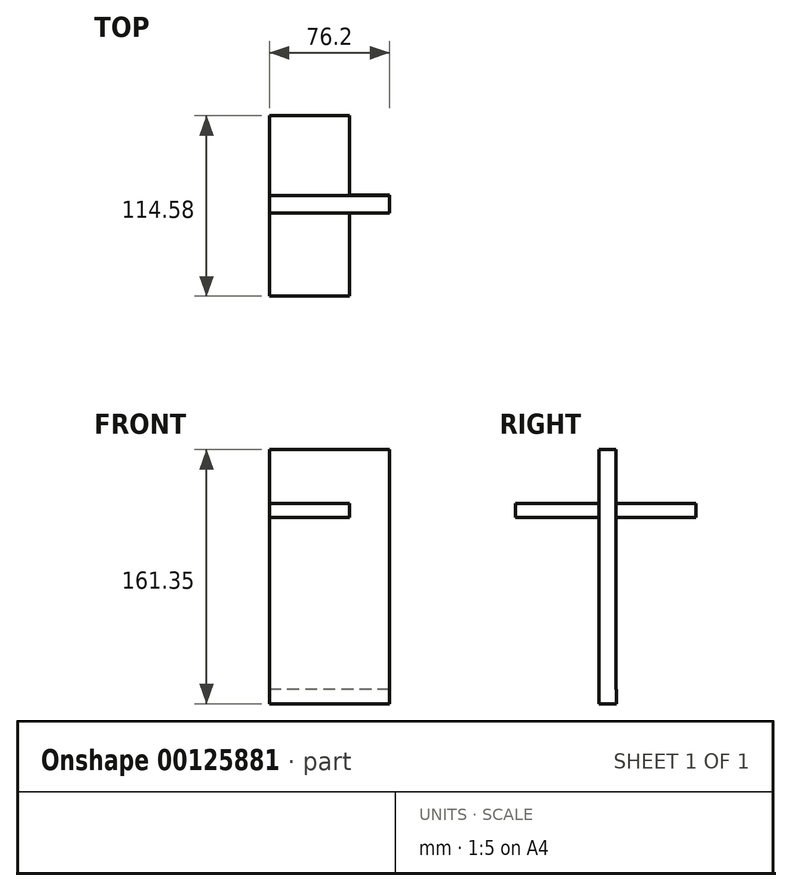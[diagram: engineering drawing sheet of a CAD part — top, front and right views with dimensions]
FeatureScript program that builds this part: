
annotation { "Feature Type Name" : "Feature", "Feature Type Description" : "" }
export const myFeature = defineFeature(function(context is Context, id is Id, definition is map)
    precondition{}
    {
        {
            var Q0;
            Q0=qCreatedBy(makeId("Right.planeOp"),FACE);
            var sketch = newSketch(context, id + "F0", { "sketchPlane" : qUnion([Q0])});
            skLineSegment(sketch, "E0.bottom", {"start": v(-22.48, 69.18) * mm, "end": v(-11.48, 69.18) * mm});
            skLineSegment(sketch, "E0.top", {"start": v(-22.48, -76.62) * mm, "end": v(-11.48, -76.62) * mm});
            skLineSegment(sketch, "E0.left", {"start": v(-22.48, 69.18) * mm, "end": v(-22.48, -76.62) * mm});
            skLineSegment(sketch, "E0.right", {"start": v(-11.48, 69.18) * mm, "end": v(-11.48, -76.62) * mm});
            skLineSegment(sketch, "E1.bottom", {"start": v(-11.48, 69.18) * mm, "end": v(-22.48, 69.18) * mm});
            skLineSegment(sketch, "E1.top", {"start": v(-11.48, 75.6) * mm, "end": v(-22.48, 75.6) * mm});
            skLineSegment(sketch, "E1.left", {"start": v(-11.48, 69.18) * mm, "end": v(-11.48, 75.6) * mm});
            skLineSegment(sketch, "E1.right", {"start": v(-22.48, 69.18) * mm, "end": v(-22.48, 75.6) * mm});
            skLineSegment(sketch, "E2.bottom", {"start": v(-22.48, -76.62) * mm, "end": v(-11.24, -76.62) * mm});
            skLineSegment(sketch, "E2.top", {"start": v(-22.48, -85.75) * mm, "end": v(-11.24, -85.75) * mm});
            skLineSegment(sketch, "E2.left", {"start": v(-22.48, -76.62) * mm, "end": v(-22.48, -85.75) * mm});
            skLineSegment(sketch, "E2.right", {"start": v(-11.24, -76.62) * mm, "end": v(-11.24, -85.75) * mm});
            skSolve(sketch);
        }
        {
            var Q0;
            Q0 = qSketchRegion(id + "F0", true);
            extrude(context, id + "F1", {"entities" : qUnion([Q0]), "depth" : 76.2 * mm});
        }
        {
            var Q0;
            Q0=qCreatedBy(makeId("Right.planeOp"),FACE);
            var sketch = newSketch(context, id + "F2", { "sketchPlane" : qUnion([Q0])});
            skLineSegment(sketch, "E3.bottom", {"start": v(-75.35, 32.45) * mm, "end": v(39.23, 32.45) * mm});
            skLineSegment(sketch, "E3.top", {"start": v(-75.35, 41.54) * mm, "end": v(39.23, 41.54) * mm});
            skLineSegment(sketch, "E3.left", {"start": v(-75.35, 32.45) * mm, "end": v(-75.35, 41.54) * mm});
            skLineSegment(sketch, "E3.right", {"start": v(39.23, 32.45) * mm, "end": v(39.23, 41.54) * mm});
            skSolve(sketch);
        }
        {
            var Q0;
            Q0=makeQuery(id+"F2.imprint","IMPRINT",FACE,{"disambiguationData":[TD([[makeQuery(id+"F2.imprint","IMPRINT",EDGE,{"derivedFrom":sQuery(id+"F2.wireOp",EDGE,"E3.bottom")}),1.0]])]});
            extrude(context, id + "F3", {"entities" : qUnion([Q0]), "operationType" : NewBodyOperationType.ADD, "depth" : 50.8 * mm});
        }
    });
